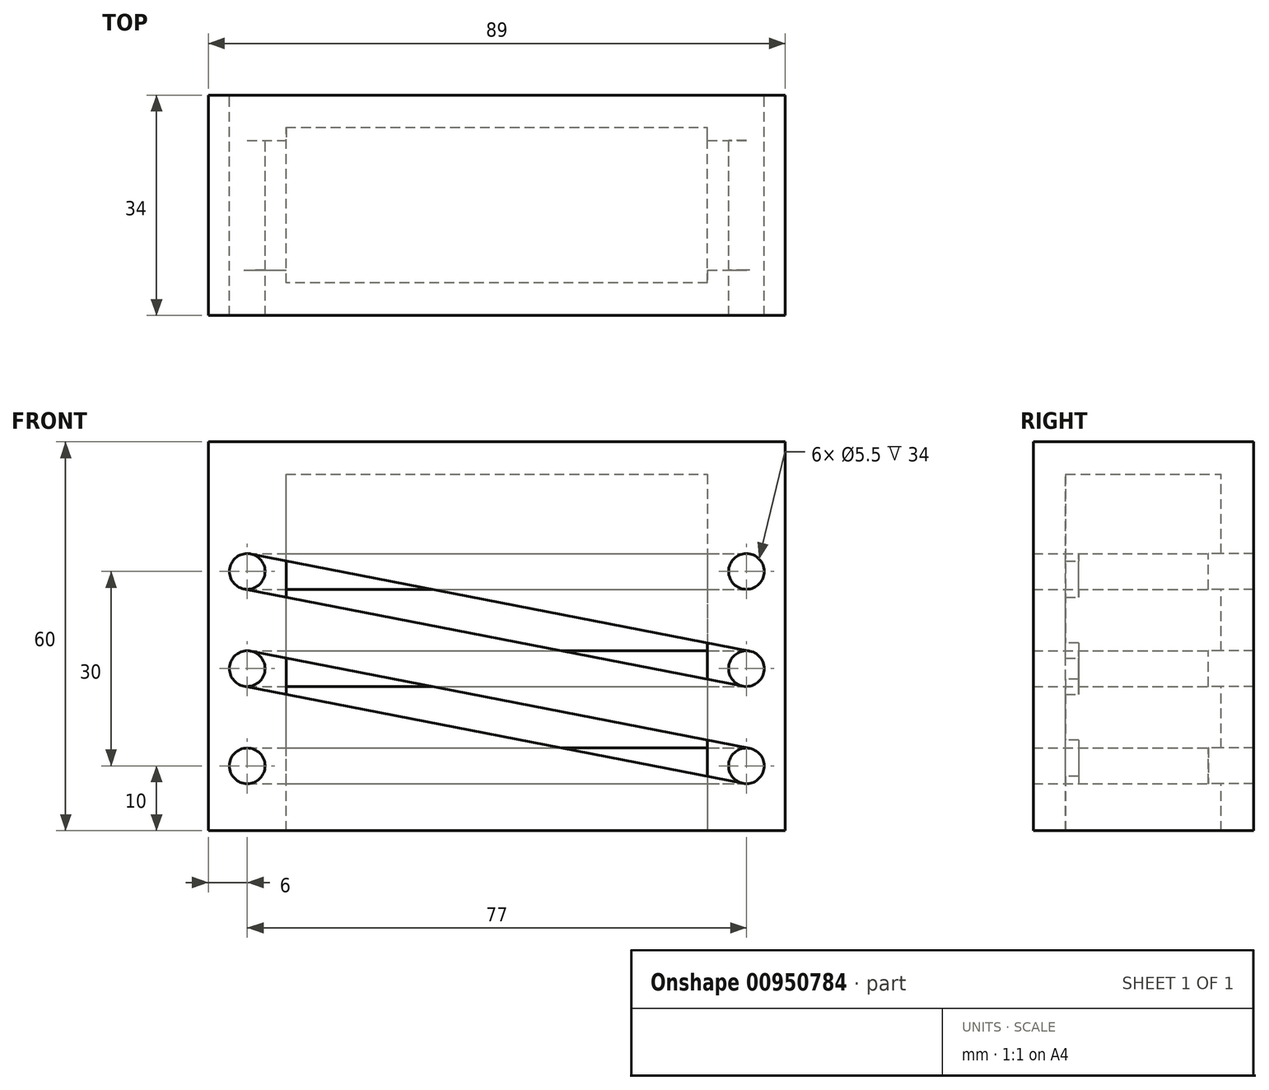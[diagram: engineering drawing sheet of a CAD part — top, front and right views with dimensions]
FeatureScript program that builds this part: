
annotation { "Feature Type Name" : "Feature", "Feature Type Description" : "" }
export const myFeature = defineFeature(function(context is Context, id is Id, definition is map)
    precondition{}
    {
        {
            var Q0;
            Q0=qCreatedBy(makeId("Front.planeOp"),FACE);
            var sketch = newSketch(context, id + "F0", { "sketchPlane" : qUnion([Q0])});
            skLineSegment(sketch, "E0.bottom", {"start": v(-77, 60) * mm, "end": v(12, 60) * mm});
            skLineSegment(sketch, "E0.top", {"start": v(-77, 0) * mm, "end": v(-65, 0) * mm});
            skLineSegment(sketch, "E0.left", {"start": v(-77, 60) * mm, "end": v(-77, 0) * mm});
            skLineSegment(sketch, "E0.right", {"start": v(12, 60) * mm, "end": v(12, 0) * mm});
            skLineSegment(sketch, "E1", {"start": v(-65, 0) * mm, "end": v(-65, 55) * mm});
            skLineSegment(sketch, "E2", {"start": v(-65, 55) * mm, "end": v(0, 55) * mm});
            skLineSegment(sketch, "E3", {"start": v(0, 55) * mm, "end": v(0, 0) * mm});
            skLineSegment(sketch, "E4.trimOffspring", {"start": v(0, 0) * mm, "end": v(12, 0) * mm});
            skSolve(sketch);
        }
        {
            var Q0;
            Q0 = qSketchRegion(id + "F0", true);
            extrude(context, id + "F1", {"entities" : qUnion([Q0]), "depth" : 24 * mm, "offsetDistance" : 25 * mm});
        }
        {
            var Q0;
            Q0=qCreatedBy(makeId("Front.planeOp"),FACE);
            var sketch = newSketch(context, id + "F2", { "sketchPlane" : qUnion([Q0])});
            skLineSegment(sketch, "E5.bottom", {"start": v(-77, 60) * mm, "end": v(12, 60) * mm});
            skLineSegment(sketch, "E5.top", {"start": v(-77, 0) * mm, "end": v(12, 0) * mm});
            skLineSegment(sketch, "E5.left", {"start": v(-77, 60) * mm, "end": v(-77, 0) * mm});
            skLineSegment(sketch, "E5.right", {"start": v(12, 60) * mm, "end": v(12, 0) * mm});
            skSolve(sketch);
        }
        {
            var Q0;
            Q0 = qSketchRegion(id + "F2", true);
            extrude(context, id + "F3", {"entities" : qUnion([Q0]), "operationType" : NewBodyOperationType.ADD, "depth" : 29 * mm, "offsetDistance" : 25 * mm, "hasSecondDirection" : true, "secondDirectionOppositeDirection" : false, "secondDirectionDepth" : 24 * mm});
        }
        {
            var Q0;
            Q0 = qSketchRegion(id + "F2", true);
            extrude(context, id + "F4", {"entities" : qUnion([Q0]), "operationType" : NewBodyOperationType.ADD, "oppositeDirection" : true, "depth" : 5 * mm, "offsetDistance" : 25 * mm});
        }
        {
            var Q0;
            Q0=qCreatedBy(makeId("Front.planeOp"),FACE);
            var sketch = newSketch(context, id + "F5", { "sketchPlane" : qUnion([Q0])});
            skCircle(sketch, "E6", {"center": v(-71, 25) * mm, "radius": 2.75 * mm});
            skCircle(sketch, "E7", {"center": v(-71, 10) * mm, "radius": 2.75 * mm});
            skCircle(sketch, "E8", {"center": v(6, 10) * mm, "radius": 2.75 * mm});
            skCircle(sketch, "E9", {"center": v(6, 25) * mm, "radius": 2.75 * mm});
            skCircle(sketch, "E10", {"center": v(6, 40) * mm, "radius": 2.75 * mm});
            skCircle(sketch, "E11", {"center": v(-71, 40) * mm, "radius": 2.75 * mm});
            skSolve(sketch);
        }
        {
            var Q0;
            Q0 = qSketchRegion(id + "F5", true);
            extrude(context, id + "F6", {"entities" : qUnion([Q0]), "operationType" : NewBodyOperationType.REMOVE, "endBound" : BoundingType.THROUGH_ALL, "depth" : 28 * mm, "offsetDistance" : 25 * mm, "hasSecondDirection" : true, "secondDirectionBound" : BoundingType.THROUGH_ALL, "secondDirectionOppositeDirection" : true, "secondDirectionDepth" : 23 * mm});
        }
        {
            var Q0;
            Q0=qCreatedBy(makeId("Front.planeOp"),FACE);
            var sketch = newSketch(context, id + "F7", { "sketchPlane" : qUnion([Q0])});
            skLineSegment(sketch, "E12.bottom", {"start": v(-71, 42.75) * mm, "end": v(6, 42.75) * mm});
            skLineSegment(sketch, "E12.top", {"start": v(-71, 37.25) * mm, "end": v(6, 37.25) * mm});
            skLineSegment(sketch, "E12.left", {"start": v(-71, 42.75) * mm, "end": v(-71, 37.25) * mm});
            skLineSegment(sketch, "E12.right", {"start": v(6, 42.75) * mm, "end": v(6, 37.25) * mm});
            skLineSegment(sketch, "E13.bottom", {"start": v(-71, 27.75) * mm, "end": v(6, 27.75) * mm});
            skLineSegment(sketch, "E13.top", {"start": v(-71, 22.25) * mm, "end": v(6, 22.25) * mm});
            skLineSegment(sketch, "E13.left", {"start": v(-71, 27.75) * mm, "end": v(-71, 22.25) * mm});
            skLineSegment(sketch, "E13.right", {"start": v(6, 27.75) * mm, "end": v(6, 22.25) * mm});
            skLineSegment(sketch, "E14.bottom", {"start": v(-71, 12.75) * mm, "end": v(6, 12.75) * mm});
            skLineSegment(sketch, "E14.top", {"start": v(-71, 7.25) * mm, "end": v(6, 7.25) * mm});
            skLineSegment(sketch, "E14.left", {"start": v(-71, 12.75) * mm, "end": v(-71, 7.25) * mm});
            skLineSegment(sketch, "E14.right", {"start": v(6, 12.75) * mm, "end": v(6, 7.25) * mm});
            skSolve(sketch);
        }
        {
            var Q0;
            Q0 = qSketchRegion(id + "F7", true);
            extrude(context, id + "F8", {"entities" : qUnion([Q0]), "operationType" : NewBodyOperationType.REMOVE, "oppositeDirection" : true, "depth" : 5 * mm, "offsetDistance" : 25 * mm, "hasSecondDirection" : true, "secondDirectionOppositeDirection" : false, "secondDirectionDepth" : 2 * mm});
        }
        {
            var Q0;
            Q0=qCreatedBy(makeId("Front.planeOp"),FACE);
            var sketch = newSketch(context, id + "F9", { "sketchPlane" : qUnion([Q0])});
            skLineSegment(sketch, "E15.bottom", {"start": v(-71.53, 22.3) * mm, "end": v(5.47, 7.3) * mm});
            skLineSegment(sketch, "E15.top", {"start": v(-70.47, 27.7) * mm, "end": v(6.53, 12.7) * mm});
            skLineSegment(sketch, "E15.left", {"start": v(-70.47, 27.7) * mm, "end": v(-71.53, 22.3) * mm});
            skLineSegment(sketch, "E15.right", {"start": v(6.53, 12.7) * mm, "end": v(5.47, 7.3) * mm});
            skLineSegment(sketch, "E16.bottom", {"start": v(-71.53, 37.3) * mm, "end": v(5.47, 22.3) * mm});
            skLineSegment(sketch, "E16.top", {"start": v(-70.47, 42.7) * mm, "end": v(6.53, 27.7) * mm});
            skLineSegment(sketch, "E16.left", {"start": v(-70.47, 42.7) * mm, "end": v(-71.53, 37.3) * mm});
            skLineSegment(sketch, "E16.right", {"start": v(6.53, 27.7) * mm, "end": v(5.47, 22.3) * mm});
            skSolve(sketch);
        }
        {
            var Q0;
            Q0 = qSketchRegion(id + "F9", true);
            extrude(context, id + "F10", {"entities" : qUnion([Q0]), "operationType" : NewBodyOperationType.REMOVE, "depth" : 29 * mm, "offsetDistance" : 25 * mm, "hasSecondDirection" : true, "secondDirectionOppositeDirection" : false, "secondDirectionDepth" : 22 * mm});
        }
    });
